# Revit family: Распределительныt коллектора ECO 2 DN25 и DN32
name_source: partatom
category: Арматура трубопроводов
units: mm (PartAtom-declared; Revit-internal decimal feet)

## family parameters
Всегда вертикально = Да
На основе рабочей плоскости = Нет
Общий = Да
При загрузке вырезать с полостями = Нет
Размер круглого соединителя = Использовать диаметр
Тип детали = Вставляется

## types (5) — shared parameters
A = 63 мм
ADSK_Единица измерения = шт.
ADSK_Завод-изготовитель = Huch EnTEC
ADSK_Количество = 1
B = 125 мм
C = 131 мм
F = 48 мм
G = 15 мм
Q max = 0 Вт
z = 121 мм
ΔT = 0 °C
Гайка = 11 мм
Группа модели = Коллекторы ECO2
Изготовитель = Huch EnTEC
Метод определения потерь = Не задано
zero-valued in all types: Отметка по умолчанию

## per-type parameters (varying)
| type | ADSK_Масса | ADSK_Наименование | ADSK_Наименование краткое | D | D1 | E | Зависимость №1 | Зависимость №2 | Консоль |
| ECO2 DN25 3-контура | 5.8 | Распределительный коллектор ECO2 DN25 на 3 отопительных контура до 120кВт | Коллектор, ECO2 DN25 3-контура | 178 мм | 25 мм | 500 мм | 4 | 2 | 250 мм |
| ECO2 DN25 5-контуров | 8.5 | Распределительный коллектор ECO2 DN25 на 5 отопительных контура до 120кВт | Коллектор, ECO2 DN25 5-контуров | 205 мм | 25 мм | 750 мм | 6 | 3 | 500 мм |
| ECO2 DN25 7-контуров | 1 | Распределительный коллектор ECO2 DN25 на 7 отопительных контура до 120кВт | Коллектор, ECO2 DN25 7-контуров | 205 мм | 25 мм | 1000 мм | 8 | 4 | 750 мм |
| ECO2 DN32 3-контура | 5.8 | Распределительный коллектор ECO2 DN32 на 3 отопительных контура до 160кВт | Коллектор, ECO2 DN32 3-контура | 178 мм | 32 мм | 500 мм | 4 | 2 | 250 мм |
| ECO2 DN32 5-контуров | 8.5 | Распределительный коллектор ECO2 DN32 на 5 отопительных контура до 160кВт | Коллектор, ECO2 DN32 5-контуров | 205 мм | 32 мм | 750 мм | 6 | 3 | 500 мм |
